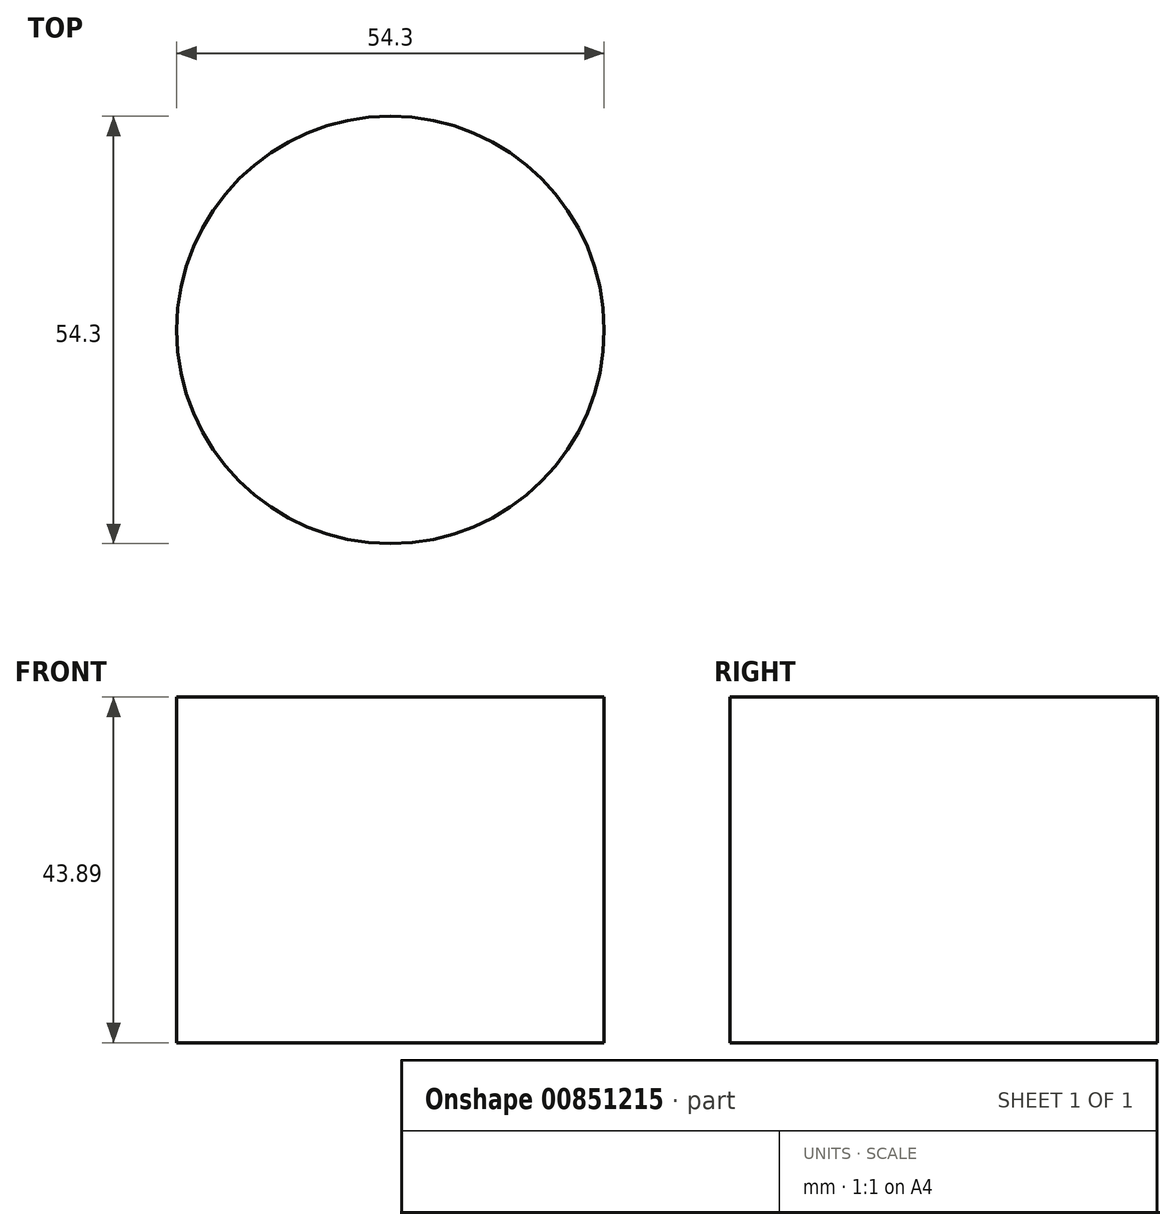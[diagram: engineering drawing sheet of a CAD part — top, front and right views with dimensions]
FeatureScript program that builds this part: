
annotation { "Feature Type Name" : "Feature", "Feature Type Description" : "" }
export const myFeature = defineFeature(function(context is Context, id is Id, definition is map)
    precondition{}
    {
        {
            var Q0;
            Q0=qCreatedBy(makeId("Top.planeOp"),FACE);
            var sketch = newSketch(context, id + "F0", { "sketchPlane" : qUnion([Q0])});
            skCircle(sketch, "E0", {"center": v(-40.58, 30.74) * mm, "radius": 27.15 * mm});
            skSolve(sketch);
        }
        {
            var Q0;
            Q0=makeQuery(id+"F0.imprint","IMPRINT",FACE,{"disambiguationData":[TD([[makeQuery(id+"F0.imprint","IMPRINT",EDGE,{"derivedFrom":sQuery(id+"F0.wireOp",EDGE,"E0")}),1.0]])]});
            extrude(context, id + "F1", {"entities" : qUnion([Q0]), "depth" : 43.9 * mm, "offsetDistance" : 25.4 * mm});
        }
    });
